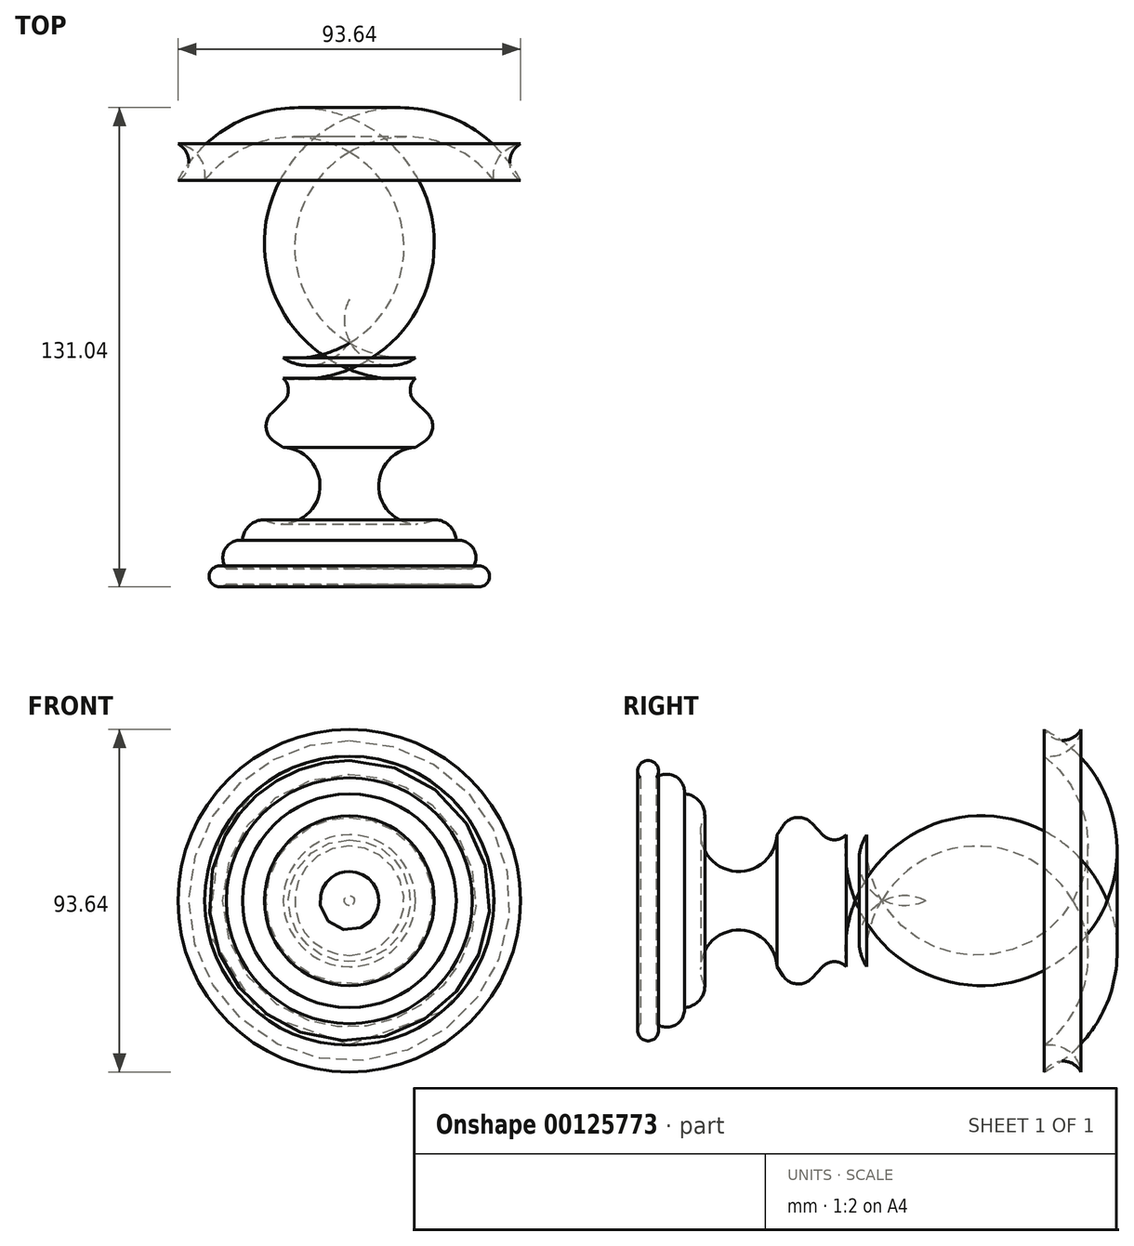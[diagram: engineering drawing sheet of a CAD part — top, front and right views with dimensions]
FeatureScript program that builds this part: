
annotation { "Feature Type Name" : "Feature", "Feature Type Description" : "" }
export const myFeature = defineFeature(function(context is Context, id is Id, definition is map)
    precondition{}
    {
        {
            var Q0;
            Q0=qCreatedBy(makeId("Top.planeOp"),FACE);
            var sketch = newSketch(context, id + "F0", { "sketchPlane" : qUnion([Q0])});
            skLineSegment(sketch, "E0", {"start": v(0, 64.15) * mm, "end": v(0, -56.3) * mm});
            skLineSegment(sketch, "E1", {"start": v(0, -56.3) * mm, "end": v(33.6, -56.3) * mm});
            skArc(sketch, "E2", {"start": v(33.6, -56.3) * mm, "mid": v(38.33, -54.13) * mm, "end": v(33.6, -51.97) * mm});
            skArc(sketch, "E3", {"start": v(33.6, -51.97) * mm, "mid": v(33.96, -46.66) * mm, "end": v(29.2, -44.24) * mm});
            skArc(sketch, "E4", {"start": v(29.2, -44.24) * mm, "mid": v(27.34, -40.23) * mm, "end": v(23.2, -38.66) * mm});
            skArc(sketch, "E5", {"start": v(18.04, -18.9) * mm, "mid": v(8.34, -31.98) * mm, "end": v(23.2, -38.66) * mm});
            skPoint(sketch, "E6", {"position": v(25.77, -13.74) * mm});
            skPoint(sketch, "E7", {"position": v(18.04, -6.44) * mm});
            skLineSegment(sketch, "E8", {"start": v(18.04, -6.44) * mm, "end": v(21.2, -9.43) * mm});
            skLineSegment(sketch, "E9", {"start": v(18.04, -18.9) * mm, "end": v(20.55, -17.23) * mm});
            skArc(sketch, "E10.filletArc", {"start": v(20.55, -17.23) * mm, "mid": v(22.76, -13.49) * mm, "end": v(21.2, -9.43) * mm});
            skArc(sketch, "E11", {"start": v(18.04, 0) * mm, "mid": v(16.65, -3.22) * mm, "end": v(18.04, -6.44) * mm});
            skArc(sketch, "E12", {"start": v(18.04, 0) * mm, "mid": v(46.7, 19.47) * mm, "end": v(46.82, 54.12) * mm});
            skArc(sketch, "E13", {"start": v(46.82, 64.15) * mm, "mid": v(43.84, 59.14) * mm, "end": v(46.82, 54.12) * mm});
            skArc(sketch, "E14", {"start": v(46.82, 64.15) * mm, "mid": v(41.03, 60.7) * mm, "end": v(39.52, 54.12) * mm});
            skArc(sketch, "E15", {"start": v(18.04, 5.61) * mm, "mid": v(43.08, 23.53) * mm, "end": v(39.52, 54.12) * mm});
            skArc(sketch, "E16", {"start": v(0, 10.3) * mm, "mid": v(7.97, 3.92) * mm, "end": v(18.04, 5.61) * mm});
            skSolve(sketch);
        }
        {
            var Q0;
            {var subQ0=sQuery(id+"F0.wireOp",EDGE,"E1");Q0=makeQuery(id+"F0.imprint","IMPRINT",FACE,{"disambiguationData":[TD([[makeQuery(id+"F0.imprint","IMPRINT",EDGE,{"derivedFrom":subQ0}),1.0]])]});}
            var Q1;
            Q1=sQuery(id+"F0.wireOp",EDGE,"E0");
            revolve(context, id + "F1", {"entities" : qUnion([Q0]), "axis" : qUnion([Q1]), "revolveType" : RevolveType.FULL});
        }
    });
